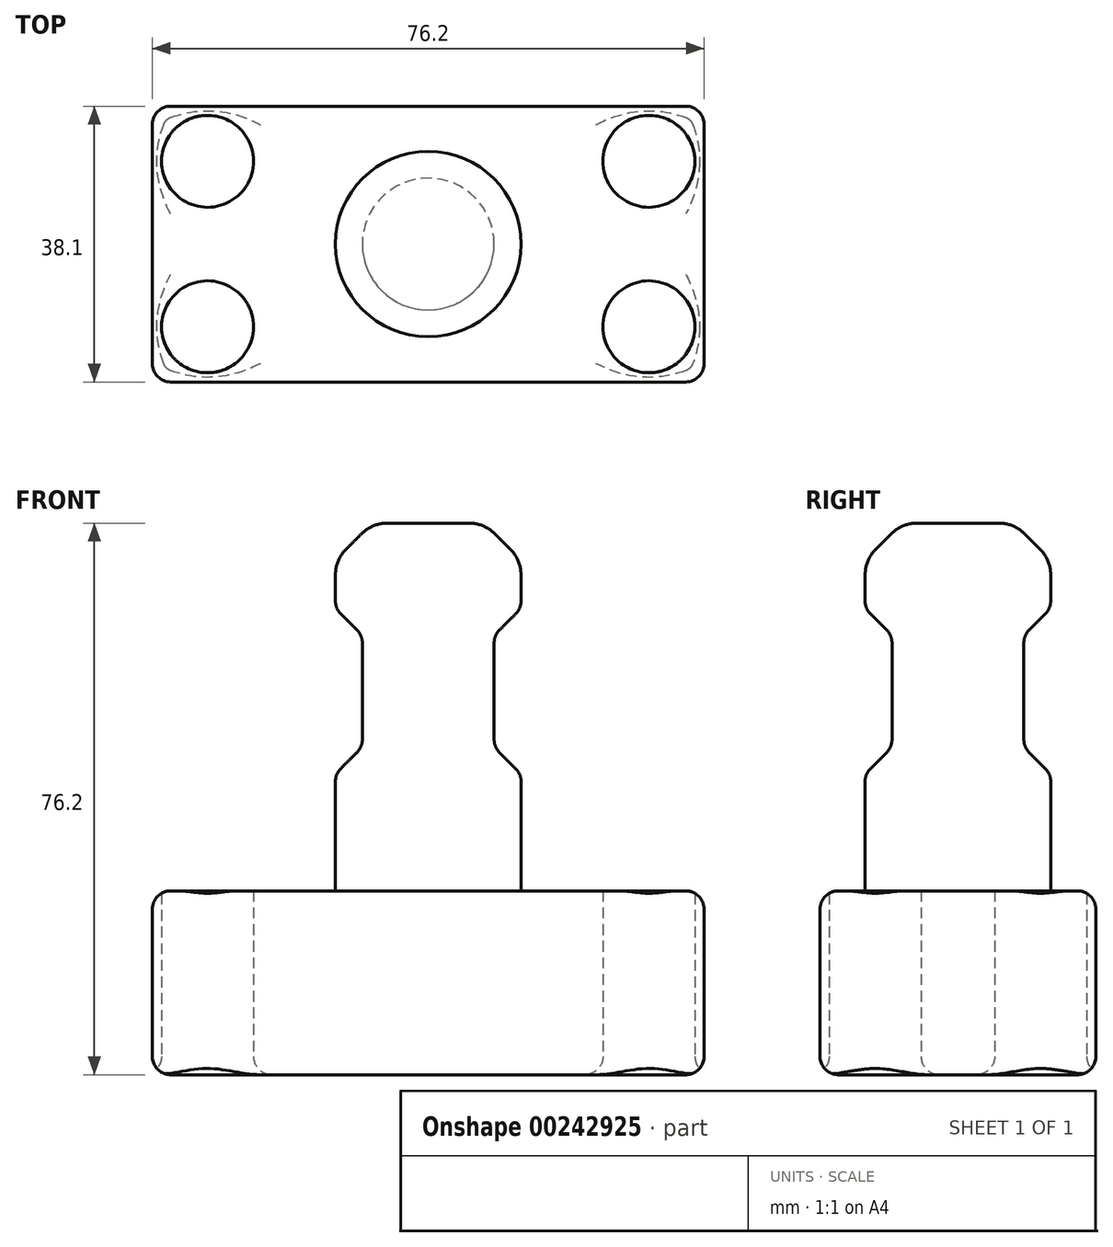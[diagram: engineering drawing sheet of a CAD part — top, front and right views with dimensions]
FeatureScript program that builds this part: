
annotation { "Feature Type Name" : "Feature", "Feature Type Description" : "" }
export const myFeature = defineFeature(function(context is Context, id is Id, definition is map)
    precondition{}
    {
        {
            var Q0;
            Q0=qCreatedBy(makeId("Top.planeOp"),FACE);
            var sketch = newSketch(context, id + "F0", { "sketchPlane" : qUnion([Q0])});
            skLineSegment(sketch, "E0.bottom", {"start": v(38.1, 19.05) * mm, "end": v(-38.1, 19.05) * mm});
            skLineSegment(sketch, "E0.top", {"start": v(38.1, -19.05) * mm, "end": v(-38.1, -19.05) * mm});
            skLineSegment(sketch, "E0.left", {"start": v(38.1, 19.05) * mm, "end": v(38.1, -19.05) * mm});
            skLineSegment(sketch, "E0.right", {"start": v(-38.1, 19.05) * mm, "end": v(-38.1, -19.05) * mm});
            skPoint(sketch, "E0.middle", {"position": v(0, 0) * mm});
            skSolve(sketch);
        }
        {
            var Q0;
            Q0 = qSketchRegion(id + "F0", true);
            extrude(context, id + "F1", {"entities" : qUnion([Q0]), "depth" : 25.4 * mm});
        }
        {
            var Q0;
            Q0=qCreatedBy(makeId("Top.planeOp"),FACE);
            var sketch = newSketch(context, id + "F2", { "sketchPlane" : qUnion([Q0])});
            skCircle(sketch, "E1", {"center": v(-30.48, 11.43) * mm, "radius": 6.35 * mm});
            skCircle(sketch, "E2", {"center": v(30.48, -11.43) * mm, "radius": 6.35 * mm});
            skCircle(sketch, "E3", {"center": v(-30.48, -11.43) * mm, "radius": 6.35 * mm});
            skCircle(sketch, "E4", {"center": v(30.48, 11.43) * mm, "radius": 6.35 * mm});
            skSolve(sketch);
        }
        {
            var Q0;
            Q0 = qSketchRegion(id + "F2", true);
            extrude(context, id + "F3", {"entities" : qUnion([Q0]), "operationType" : NewBodyOperationType.REMOVE, "depth" : 25.4 * mm});
        }
        {
            var Q0;
            Q0=makeQuery(id+"F1.opExtrude","CAP_FACE",FACE,{"disambiguationData":[OSD([sQuery(id+"F0.wireOp",EDGE,"E0.bottom"),sQuery(id+"F0.wireOp",EDGE,"E0.top"),sQuery(id+"F0.wireOp",EDGE,"E0.left"),sQuery(id+"F0.wireOp",EDGE,"E0.right")])],"isStart":false});
            var sketch = newSketch(context, id + "F4", { "sketchPlane" : qUnion([Q0])});
            skCircle(sketch, "E5", {"center": v(0, 0) * mm, "radius": 12.82 * mm});
            skSolve(sketch);
        }
        {
            var Q0;
            Q0 = qSketchRegion(id + "F4", true);
            extrude(context, id + "F5", {"entities" : qUnion([Q0]), "operationType" : NewBodyOperationType.ADD, "depth" : 50.8 * mm});
        }
        {
            var Q0;
            Q0=qCreatedBy(makeId("Front.planeOp"),FACE);
            var sketch = newSketch(context, id + "F6", { "sketchPlane" : qUnion([Q0])});
            skLineSegment(sketch, "E6.bottom", {"start": v(-21.8, 59.33) * mm, "end": v(-9.1, 59.33) * mm});
            skLineSegment(sketch, "E6.top", {"start": v(-21.8, 46.63) * mm, "end": v(-9.1, 46.63) * mm});
            skLineSegment(sketch, "E6.left", {"start": v(-21.8, 59.33) * mm, "end": v(-21.8, 46.63) * mm});
            skLineSegment(sketch, "E6.right", {"start": v(-9.1, 59.33) * mm, "end": v(-9.1, 46.63) * mm});
            skSolve(sketch);
        }
        {
            var Q0;
            Q0=makeQuery(id+"F6.imprint","IMPRINT",FACE,{"disambiguationData":[TD([[makeQuery(id+"F6.imprint","IMPRINT",EDGE,{"derivedFrom":sQuery(id+"F6.wireOp",EDGE,"E6.bottom")}),-1.0]])]});
            var Q1;
            Q1=makeQuery(id+"F5.opExtrude","CAP_EDGE",EDGE,{"disambiguationData":[OSD([sQuery(id+"F4.wireOp",EDGE,"E5")])],"isStart":false});
            revolve(context, id + "F7", {"operationType" : NewBodyOperationType.REMOVE, "entities" : qUnion([Q0]), "axis" : qUnion([Q1]), "revolveType" : RevolveType.FULL, "oppositeDirection" : true});
        }
        {
            var Q0;
            Q0=makeQuery(id+"F7.boolean.opBoolean","INTERSECT",EDGE,{"derivedFrom":[makeQuery(id+"F5.opExtrude","SWEPT_FACE",FACE,{"disambiguationData":[OSD([sQuery(id+"F4.wireOp",EDGE,"E5")])]}),makeQuery(id+"F7.opRevolve","SWEPT_FACE",FACE,{"disambiguationData":[OSD([sQuery(id+"F6.wireOp",EDGE,"E6.top")])]})]});
            var Q1;
            Q1=makeQuery(id+"F7.boolean.opBoolean","INTERSECT",EDGE,{"derivedFrom":[makeQuery(id+"F5.opExtrude","SWEPT_FACE",FACE,{"disambiguationData":[OSD([sQuery(id+"F4.wireOp",EDGE,"E5")])]}),makeQuery(id+"F7.opRevolve","SWEPT_FACE",FACE,{"disambiguationData":[OSD([sQuery(id+"F6.wireOp",EDGE,"E6.bottom")])]})]});
            var Q2;
            Q2=makeQuery(id+"F5.opExtrude","CAP_EDGE",EDGE,{"disambiguationData":[OSD([sQuery(id+"F4.wireOp",EDGE,"E5")])],"isStart":true});
            var Q3;
            Q3=makeQuery(id+"F5.opExtrude","CAP_EDGE",EDGE,{"disambiguationData":[OSD([sQuery(id+"F4.wireOp",EDGE,"E5")])],"isStart":false});
            chamfer(context, id + "F8", {"entities" : qUnion([Q0, Q1, Q2, Q3]), "width" : 5.08 * mm, "tangentPropagation" : true});
        }
        {
            var Q0;
            Q0=makeQuery(id+"F8.opChamfer","BLEND_FACE",FACE,{"disambiguationData":[OSD([sQuery(id+"F4.wireOp",EDGE,"E5"),sQuery(id+"F6.wireOp",EDGE,"E6.top")])]});
            var Q1;
            {var subQ0=sQuery(id+"F4.wireOp",EDGE,"E5");var subQ1=makeQuery(id+"F7.opRevolve","SWEPT_FACE",FACE,{"disambiguationData":[OSD([sQuery(id+"F6.wireOp",EDGE,"E6.bottom")])]});var subQ2=makeQuery(id+"F5.opExtrude","SWEPT_FACE",FACE,{"disambiguationData":[OSD([subQ0])]});Q1=makeQuery(id+"F8.opChamfer","BLEND_EDGE",EDGE,{"blendedFrom":[makeQuery(id+"F7.boolean.opBoolean","INTERSECT",EDGE,{"derivedFrom":[subQ2,subQ1]}),makeQuery(id+"F7.boolean.opBoolean","SPLIT",FACE,{"disambiguationData":[TD([makeQuery(id+"F5.opExtrude","CAP_FACE",FACE,{"disambiguationData":[OSD([subQ0])],"isStart":false})])],"derivedFrom":subQ2})],"blendedInto":[makeQuery(id+"F7.boolean.opBoolean","SPLIT",FACE,{"disambiguationData":[TD([makeQuery(id+"F5.opExtrude","CAP_FACE",FACE,{"disambiguationData":[OSD([subQ0])],"isStart":false})])],"derivedFrom":subQ2})]});}
            var Q2;
            Q2=makeQuery(id+"F8.opChamfer","BLEND_EDGE",EDGE,{"blendedFrom":[makeQuery(id+"F7.boolean.opBoolean","INTERSECT",EDGE,{"derivedFrom":[makeQuery(id+"F5.opExtrude","SWEPT_FACE",FACE,{"disambiguationData":[OSD([sQuery(id+"F4.wireOp",EDGE,"E5")])]}),makeQuery(id+"F7.opRevolve","SWEPT_FACE",FACE,{"disambiguationData":[OSD([sQuery(id+"F6.wireOp",EDGE,"E6.bottom")])]})]}),makeQuery(id+"F7.boolean.opBoolean","COPY",FACE,{"derivedFrom":makeQuery(id+"F7.opRevolve","SWEPT_FACE",FACE,{"disambiguationData":[OSD([sQuery(id+"F6.wireOp",EDGE,"E6.right")])]})})],"blendedInto":[makeQuery(id+"F7.boolean.opBoolean","COPY",FACE,{"derivedFrom":makeQuery(id+"F7.opRevolve","SWEPT_FACE",FACE,{"disambiguationData":[OSD([sQuery(id+"F6.wireOp",EDGE,"E6.right")])]})})]});
            var Q3;
            Q3=makeQuery(id+"F8.opChamfer","BLEND_EDGE",EDGE,{"blendedFrom":[makeQuery(id+"F7.boolean.opBoolean","INTERSECT",EDGE,{"derivedFrom":[makeQuery(id+"F5.opExtrude","SWEPT_FACE",FACE,{"disambiguationData":[OSD([sQuery(id+"F4.wireOp",EDGE,"E5")])]}),makeQuery(id+"F7.opRevolve","SWEPT_FACE",FACE,{"disambiguationData":[OSD([sQuery(id+"F6.wireOp",EDGE,"E6.top")])]})]}),makeQuery(id+"F7.boolean.opBoolean","COPY",FACE,{"derivedFrom":makeQuery(id+"F7.opRevolve","SWEPT_FACE",FACE,{"disambiguationData":[OSD([sQuery(id+"F6.wireOp",EDGE,"E6.right")])]})})],"blendedInto":[makeQuery(id+"F7.boolean.opBoolean","COPY",FACE,{"derivedFrom":makeQuery(id+"F7.opRevolve","SWEPT_FACE",FACE,{"disambiguationData":[OSD([sQuery(id+"F6.wireOp",EDGE,"E6.right")])]})})]});
            var Q4;
            Q4=makeQuery(id+"F3.boolean.opBoolean","COPY",EDGE,{"derivedFrom":makeQuery(id+"F3.opExtrude","CAP_EDGE",EDGE,{"disambiguationData":[OSD([sQuery(id+"F2.wireOp",EDGE,"E3")])],"isStart":false})});
            var Q5;
            Q5=makeQuery(id+"F3.boolean.opBoolean","COPY",EDGE,{"derivedFrom":makeQuery(id+"F3.opExtrude","CAP_EDGE",EDGE,{"disambiguationData":[OSD([sQuery(id+"F2.wireOp",EDGE,"E1")])],"isStart":false})});
            var Q6;
            Q6=makeQuery(id+"F3.boolean.opBoolean","COPY",EDGE,{"derivedFrom":makeQuery(id+"F3.opExtrude","CAP_EDGE",EDGE,{"disambiguationData":[OSD([sQuery(id+"F2.wireOp",EDGE,"E4")])],"isStart":false})});
            var Q7;
            Q7=makeQuery(id+"F3.boolean.opBoolean","COPY",EDGE,{"derivedFrom":makeQuery(id+"F3.opExtrude","CAP_EDGE",EDGE,{"disambiguationData":[OSD([sQuery(id+"F2.wireOp",EDGE,"E2")])],"isStart":false})});
            var Q8;
            Q8=makeQuery(id+"F1.opExtrude","CAP_EDGE",EDGE,{"disambiguationData":[OSD([sQuery(id+"F0.wireOp",EDGE,"E0.top")])],"isStart":false});
            var Q9;
            Q9=makeQuery(id+"F1.opExtrude","SWEPT_EDGE",EDGE,{"disambiguationData":[OSD([sQuery(id+"F0.wireOp",EDGE,"E0.bottom"),sQuery(id+"F0.wireOp",EDGE,"E0.left")])]});
            var Q10;
            Q10=makeQuery(id+"F1.opExtrude","CAP_EDGE",EDGE,{"disambiguationData":[OSD([sQuery(id+"F0.wireOp",EDGE,"E0.bottom")])],"isStart":false});
            var Q11;
            Q11=makeQuery(id+"F1.opExtrude","CAP_EDGE",EDGE,{"disambiguationData":[OSD([sQuery(id+"F0.wireOp",EDGE,"E0.left")])],"isStart":false});
            var Q12;
            Q12=makeQuery(id+"F1.opExtrude","SWEPT_FACE",FACE,{"disambiguationData":[OSD([sQuery(id+"F0.wireOp",EDGE,"E0.right")])]});
            var Q13;
            Q13=makeQuery(id+"F1.opExtrude","SWEPT_FACE",FACE,{"disambiguationData":[OSD([sQuery(id+"F0.wireOp",EDGE,"E0.top")])]});
            var Q14;
            Q14=makeQuery(id+"F1.opExtrude","CAP_FACE",FACE,{"disambiguationData":[OSD([sQuery(id+"F0.wireOp",EDGE,"E0.bottom"),sQuery(id+"F0.wireOp",EDGE,"E0.top"),sQuery(id+"F0.wireOp",EDGE,"E0.left"),sQuery(id+"F0.wireOp",EDGE,"E0.right")])],"isStart":true});
            var Q15;
            {var subQ0=sQuery(id+"F4.wireOp",EDGE,"E5");Q15=makeQuery(id+"F8.opChamfer","BLEND_EDGE",EDGE,{"blendedFrom":[makeQuery(id+"F5.opExtrude","CAP_EDGE",EDGE,{"disambiguationData":[OSD([subQ0])],"isStart":true}),makeQuery(id+"F7.boolean.opBoolean","SPLIT",FACE,{"disambiguationData":[TD([makeQuery(id+"F7.opRevolve","SWEPT_FACE",FACE,{"disambiguationData":[OSD([sQuery(id+"F6.wireOp",EDGE,"E6.top")])]})])],"derivedFrom":makeQuery(id+"F5.opExtrude","SWEPT_FACE",FACE,{"disambiguationData":[OSD([subQ0])]})})],"blendedInto":[makeQuery(id+"F7.boolean.opBoolean","SPLIT",FACE,{"disambiguationData":[TD([makeQuery(id+"F7.opRevolve","SWEPT_FACE",FACE,{"disambiguationData":[OSD([sQuery(id+"F6.wireOp",EDGE,"E6.top")])]})])],"derivedFrom":makeQuery(id+"F5.opExtrude","SWEPT_FACE",FACE,{"disambiguationData":[OSD([subQ0])]})})]});}
            fillet(context, id + "F9", {"entities" : qUnion([Q0, Q1, Q2, Q3, Q4, Q5, Q6, Q7, Q8, Q9, Q10, Q11, Q12, Q13, Q14, Q15]), "radius" : 2.54 * mm, "tangentPropagation" : true, "allowEdgeOverflow" : false});
        }
        {
            var Q0;
            Q0=makeQuery(id+"F8.opChamfer","BLEND_FACE",FACE,{"disambiguationData":[OSD([sQuery(id+"F4.wireOp",EDGE,"E5")])]});
            fillet(context, id + "F10", {"entities" : qUnion([Q0]), "radius" : 5.08 * mm, "tangentPropagation" : true, "allowEdgeOverflow" : false});
        }
    });
